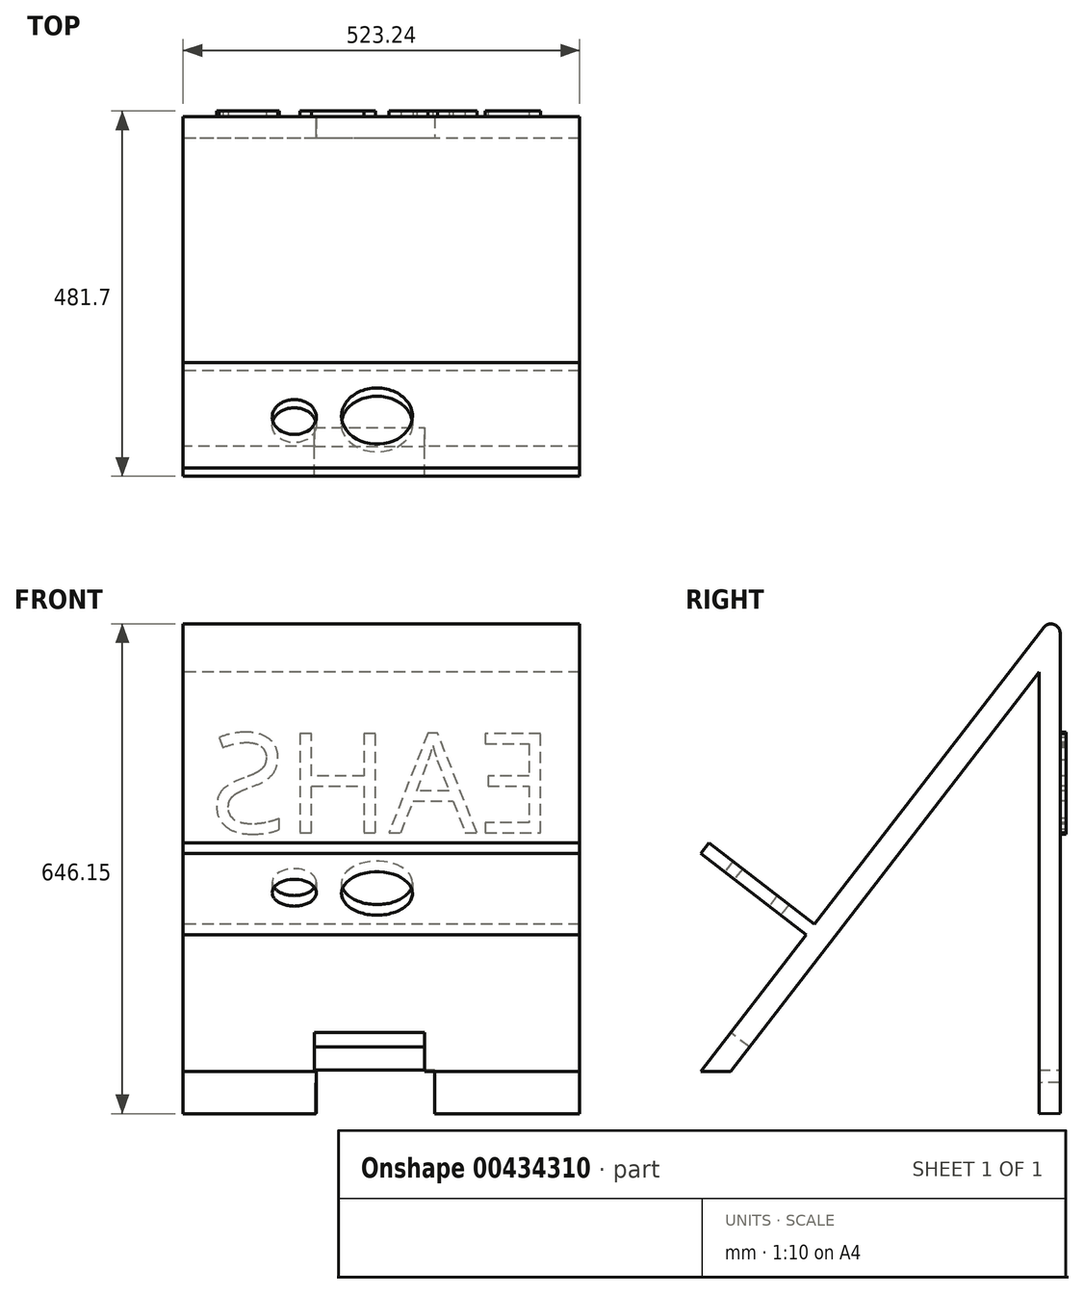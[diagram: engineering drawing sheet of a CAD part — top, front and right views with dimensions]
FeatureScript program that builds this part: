
annotation { "Feature Type Name" : "Feature", "Feature Type Description" : "" }
export const myFeature = defineFeature(function(context is Context, id is Id, definition is map)
    precondition{}
    {
        {
            var Q0;
            Q0=qCreatedBy(makeId("Right.planeOp"),FACE);
            var sketch = newSketch(context, id + "F0", { "sketchPlane" : qUnion([Q0])});
            skLineSegment(sketch, "E0", {"start": v(181.71, 192.74) * mm, "end": v(181.71, -420.93) * mm});
            skLineSegment(sketch, "E1", {"start": v(181.71, 192.74) * mm, "end": v(-292.37, -420.93) * mm});
            skLineSegment(sketch, "E2", {"start": v(-153.26, -240.86) * mm, "end": v(-292.37, -133.4) * mm});
            skLineSegment(sketch, "E3", {"start": v(-292.37, -133.4) * mm, "end": v(-281.57, -119.42) * mm});
            skLineSegment(sketch, "E4", {"start": v(-142.46, -226.88) * mm, "end": v(-281.57, -119.42) * mm});
            skLineSegment(sketch, "E5", {"start": v(181.71, -420.93) * mm, "end": v(181.71, -476.44) * mm});
            skLineSegment(sketch, "E6", {"start": v(-292.37, -420.93) * mm, "end": v(-253.1, -420.93) * mm});
            skLineSegment(sketch, "E7", {"start": v(-253.1, -420.93) * mm, "end": v(153.65, 105.58) * mm});
            skLineSegment(sketch, "E8", {"start": v(153.65, 105.58) * mm, "end": v(153.65, -476.8) * mm});
            skLineSegment(sketch, "E9", {"start": v(153.65, -476.8) * mm, "end": v(181.71, -476.44) * mm});
            skSolve(sketch);
        }
        {
            var Q0;
            Q0 = qSketchRegion(id + "F0", true);
            extrude(context, id + "F1", {"entities" : qUnion([Q0]), "depth" : 241.3 * mm, "offsetDistance" : 25.4 * mm, "hasSecondDirection" : true, "secondDirectionOppositeDirection" : true, "secondDirectionDepth" : 281.94 * mm});
        }
        {
            var Q0;
            Q0=makeQuery(id+"F1.opExtrude","SWEPT_FACE",FACE,{"disambiguationData":[OSD([sQuery(id+"F0.wireOp",EDGE,"E2")])]});
            var sketch = newSketch(context, id + "F2", { "sketchPlane" : qUnion([Q0])});
            skCircle(sketch, "E10", {"center": v(-26.1, 63.3) * mm, "radius": 46.8 * mm});
            skCircle(sketch, "E11", {"center": v(-135.2, 64.96) * mm, "radius": 29.08 * mm});
            skSolve(sketch);
        }
        {
            var Q0;
            Q0 = qSketchRegion(id + "F2", true);
            extrude(context, id + "F3", {"entities" : qUnion([Q0]), "operationType" : NewBodyOperationType.REMOVE, "oppositeDirection" : true, "depth" : 86.36 * mm, "offsetDistance" : 25.4 * mm});
        }
        {
            var Q0;
            {var subQ0=sQuery(id+"F0.wireOp",EDGE,"E1");Q0=makeQuery(id+"F1.opExtrude","SWEPT_FACE",FACE,{"disambiguationData":[OSD([subQ0]),TDD([makeQuery(id+"F0.imprint","IMPRINT",EDGE,{"disambiguationData":[TD([[makeQuery(id+"F0.imprint","INTERSECT",VERTEX,{"derivedFrom":[subQ0,sQuery(id+"F0.wireOp",EDGE,"E6")]}),1.0]])],"derivedFrom":subQ0})])]});}
            var sketch = newSketch(context, id + "F4", { "sketchPlane" : qUnion([Q0])});
            skLineSegment(sketch, "E12.bottom", {"start": v(-108.9, -511.85) * mm, "end": v(36.45, -511.85) * mm});
            skLineSegment(sketch, "E12.top", {"start": v(-108.9, -447.28) * mm, "end": v(36.45, -447.28) * mm});
            skLineSegment(sketch, "E12.left", {"start": v(-108.9, -511.85) * mm, "end": v(-108.9, -447.28) * mm});
            skLineSegment(sketch, "E12.right", {"start": v(36.45, -511.85) * mm, "end": v(36.45, -447.28) * mm});
            skSolve(sketch);
        }
        {
            var Q0;
            Q0 = qSketchRegion(id + "F4", true);
            extrude(context, id + "F5", {"entities" : qUnion([Q0]), "operationType" : NewBodyOperationType.REMOVE, "oppositeDirection" : true, "depth" : 78.74 * mm, "offsetDistance" : 25.4 * mm});
        }
        {
            var Q0;
            Q0=makeQuery(id+"F1.opExtrude","SWEPT_FACE",FACE,{"disambiguationData":[OSD([sQuery(id+"F0.wireOp",EDGE,"E0"),sQuery(id+"F0.wireOp",EDGE,"E5")])]});
            var sketch = newSketch(context, id + "F6", { "sketchPlane" : qUnion([Q0])});
            skLineSegment(sketch, "E13.bottom", {"start": v(-50.1, -476.44) * mm, "end": v(106.12, -476.44) * mm});
            skLineSegment(sketch, "E13.top", {"start": v(-50.1, -419.26) * mm, "end": v(106.12, -419.26) * mm});
            skLineSegment(sketch, "E13.left", {"start": v(-50.1, -476.44) * mm, "end": v(-50.1, -419.26) * mm});
            skLineSegment(sketch, "E13.right", {"start": v(106.12, -476.44) * mm, "end": v(106.12, -419.26) * mm});
            skSolve(sketch);
        }
        {
            var Q0;
            Q0 = qSketchRegion(id + "F6", true);
            extrude(context, id + "F7", {"entities" : qUnion([Q0]), "operationType" : NewBodyOperationType.REMOVE, "oppositeDirection" : true, "depth" : 81.28 * mm, "offsetDistance" : 25.4 * mm});
        }
        {
            var Q0;
            Q0=makeQuery(id+"F1.opExtrude","SWEPT_FACE",FACE,{"disambiguationData":[OSD([sQuery(id+"F0.wireOp",EDGE,"E9")])]});
            var sketch = newSketch(context, id + "F8", { "sketchPlane" : qUnion([Q0])});
            skLineSegment(sketch, "E14.bottom", {"start": v(50.1, -175.62) * mm, "end": v(-106.8, -175.62) * mm});
            skLineSegment(sketch, "E14.top", {"start": v(50.1, -147.56) * mm, "end": v(-106.8, -147.56) * mm});
            skLineSegment(sketch, "E14.left", {"start": v(50.1, -175.62) * mm, "end": v(50.1, -147.56) * mm});
            skLineSegment(sketch, "E14.right", {"start": v(-106.8, -175.62) * mm, "end": v(-106.8, -147.56) * mm});
            skSolve(sketch);
        }
        {
            var Q0;
            Q0 = qSketchRegion(id + "F8", true);
            extrude(context, id + "F9", {"entities" : qUnion([Q0]), "operationType" : NewBodyOperationType.REMOVE, "oppositeDirection" : true, "depth" : 40.64 * mm, "offsetDistance" : 25.4 * mm});
        }
        {
            var Q0;
            Q0=makeQuery(id+"F1.opExtrude","SWEPT_FACE",FACE,{"disambiguationData":[OSD([sQuery(id+"F0.wireOp",EDGE,"E0"),sQuery(id+"F0.wireOp",EDGE,"E5")])]});
            var sketch = newSketch(context, id + "F10", { "sketchPlane" : qUnion([Q0])});
            skText(sketch, "E15", { "text": "EAHS", "fontName": "OpenSans-Regular.ttf"});
            const initialGuessF10  = {"E15": [-0.20774, -0.10625, 1, 0, 0.13207]};
            skSetInitialGuess(sketch, initialGuessF10);
            skSolve(sketch);
        }
        {
            var Q0;
            Q0 = qSketchRegion(id + "F10", true);
            extrude(context, id + "F11", {"entities" : qUnion([Q0]), "operationType" : NewBodyOperationType.ADD, "depth" : 7.62 * mm, "offsetDistance" : 25.4 * mm});
        }
        {
            var Q0;
            Q0=makeQuery(id+"F1.opExtrude","SWEPT_EDGE",EDGE,{"disambiguationData":[OSD([sQuery(id+"F0.wireOp",EDGE,"E0"),sQuery(id+"F0.wireOp",EDGE,"E1")])]});
            fillet(context, id + "F12", {"entities" : qUnion([Q0]), "radius" : 12.12 * mm, "tangentPropagation" : true, "allowEdgeOverflow" : false});
        }
    });
